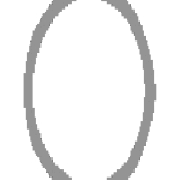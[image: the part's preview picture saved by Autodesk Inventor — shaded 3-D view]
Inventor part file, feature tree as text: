
AUTODESK INVENTOR PART (.ipt)
format: ipt  version: 2021 (Build 250183000, 183)  size: 143,360 bytes
history: native  units: in
note: dims shown in document units (in); Inventor stores cm internally (conversion verified against a paired STEP export)
features: plane x7, sketch x5, other x4, extrude x2, boolean_combine x2
ambient origin geometry x8: Origin, YZ Plane, XZ Plane, XY Plane, X Axis, Y Axis, Z Axis, Center Point
bodies: Solid1 (feature_tree), Body (feature_tree), Solid2 (feature_tree), Solid3 (feature_tree)
feature tree (20):
  other  "Driven Length"
  other  "Frame Generator"
  other  "Start Plane"
  other  "End Plane"
  plane  "Work Plane4"
  plane  "Work Plane5"
  plane  "Work Plane6"
  extrude  "Extrusion3"  Depth=0.065in
  boolean_combine  "Combine1"
  plane  "Work Plane7"
  plane  "Work Plane8"
  plane  "Work Plane9"
  extrude  "Extrusion4"  TaperAngle=0.0deg  [1 undecoded]
  boolean_combine  "Combine2"
  sketch  "Sketch"  dims[d8=90.0deg d9=6.7082in d10=0.12in d11=0.0in d12=0.12in d13=0.0in]
  sketch  "Sketch2"  dims[d0=1.0in d1=0.065in]
  plane  "Work Plane3"
  sketch  "Sketch3"  dims[d2=6.7082in d4=-0.0in]
  sketch  "Sketch4"  dims[d5=6.7082in]
  sketch  "Sketch5"  dims[d6=0.12in d7=0.0in]
note: 1 required parameter value undecoded (feature->parameter linkage not recoverable at this tier; creation-order binding heuristic only, values carry confidence <= 0.55)
